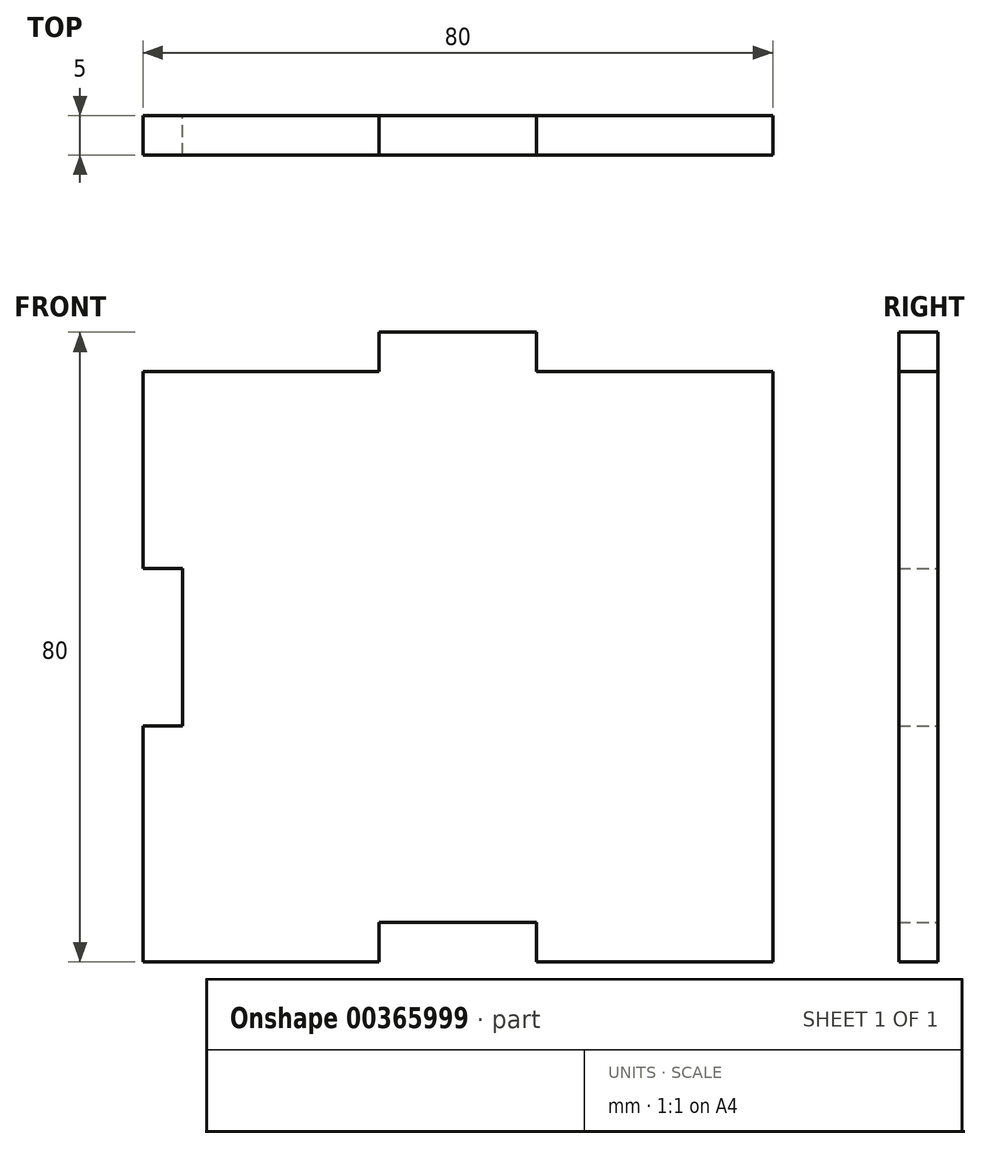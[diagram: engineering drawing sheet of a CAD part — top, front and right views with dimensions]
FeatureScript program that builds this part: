
annotation { "Feature Type Name" : "Feature", "Feature Type Description" : "" }
export const myFeature = defineFeature(function(context is Context, id is Id, definition is map)
    precondition{}
    {
        {
            var Q0;
            Q0=qCreatedBy(makeId("Front.planeOp"),FACE);
            var sketch = newSketch(context, id + "F0", { "sketchPlane" : qUnion([Q0])});
            skLineSegment(sketch, "E0", {"start": v(0, 0) * mm, "end": v(-30, 0) * mm});
            skLineSegment(sketch, "E1", {"start": v(-30, 0) * mm, "end": v(-30, 5) * mm});
            skLineSegment(sketch, "E2", {"start": v(-30, 5) * mm, "end": v(-50, 5) * mm});
            skLineSegment(sketch, "E3", {"start": v(-50, 5) * mm, "end": v(-50, 0) * mm});
            skLineSegment(sketch, "E4", {"start": v(-50, 0) * mm, "end": v(-80, 0) * mm});
            skLineSegment(sketch, "E5", {"start": v(-80, 0) * mm, "end": v(-80, 30) * mm});
            skLineSegment(sketch, "E6", {"start": v(-80, 30) * mm, "end": v(-75, 30) * mm});
            skLineSegment(sketch, "E7", {"start": v(-75, 30) * mm, "end": v(-75, 50) * mm});
            skLineSegment(sketch, "E8", {"start": v(-75, 50) * mm, "end": v(-80, 50) * mm});
            skLineSegment(sketch, "E9", {"start": v(-80, 50) * mm, "end": v(-80, 75) * mm});
            skLineSegment(sketch, "E10", {"start": v(-80, 75) * mm, "end": v(-50, 75) * mm});
            skLineSegment(sketch, "E11", {"start": v(-50, 75) * mm, "end": v(-50, 80) * mm});
            skLineSegment(sketch, "E12", {"start": v(-50, 80) * mm, "end": v(-30, 80) * mm});
            skLineSegment(sketch, "E13", {"start": v(-30, 80) * mm, "end": v(-30, 75) * mm});
            skLineSegment(sketch, "E14", {"start": v(-30, 75) * mm, "end": v(0, 75) * mm});
            skLineSegment(sketch, "E15", {"start": v(0, 75) * mm, "end": v(0, 0) * mm});
            skSolve(sketch);
        }
        {
            var Q0;
            Q0=makeQuery(id+"F0.imprint","IMPRINT",FACE,{"disambiguationData":[TD([[makeQuery(id+"F0.imprint","IMPRINT",EDGE,{"derivedFrom":sQuery(id+"F0.wireOp",EDGE,"E0")}),-1.0]])]});
            extrude(context, id + "F1", {"entities" : qUnion([Q0]), "depth" : 5 * mm});
        }
    });
